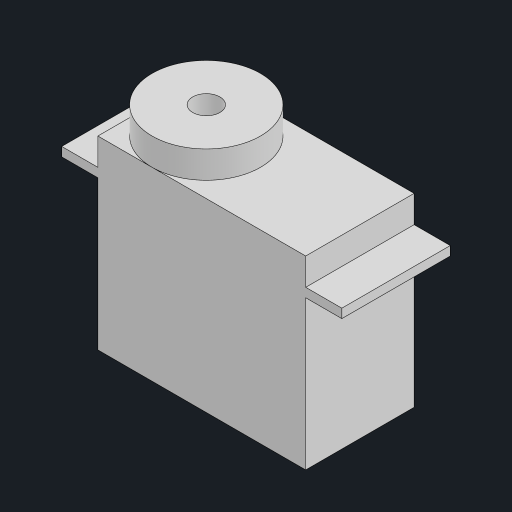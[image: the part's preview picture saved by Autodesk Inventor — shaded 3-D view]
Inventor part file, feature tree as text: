
AUTODESK INVENTOR PART (.ipt)
format: ipt  version: 2023 (Build 270158000, 158)  size: 129,024 bytes
history: native  units: in
note: dims shown in document units (in); Inventor stores cm internally (conversion verified against a paired STEP export)
features: sketch x5, extrude x4, other x1, hole x1
ambient origin geometry x8: Origin, YZ Plane, XZ Plane, XY Plane, X Axis, Y Axis, Z Axis, Center Point
bodies: Body1 (feature_tree)
feature tree (11):
  other  "ソリッド1"
  sketch  "スケッチ1"
  extrude  "押し出し1"  Depth=0.9055in
  extrude  "押し出し2"  Depth=0.4724in
  extrude  "押し出し3"  Depth=0.6496in TaperAngle=0.0deg
  extrude  "押し出し4"  Depth=0.1575in
  hole  "穴1"  [1 undecoded]
  sketch  "スケッチ2"
  sketch  "スケッチ3"
  sketch  "スケッチ4"
  sketch  "スケッチ5"
note: 1 required parameter value undecoded (feature->parameter linkage not recoverable at this tier; creation-order binding heuristic only, values carry confidence <= 0.55)
